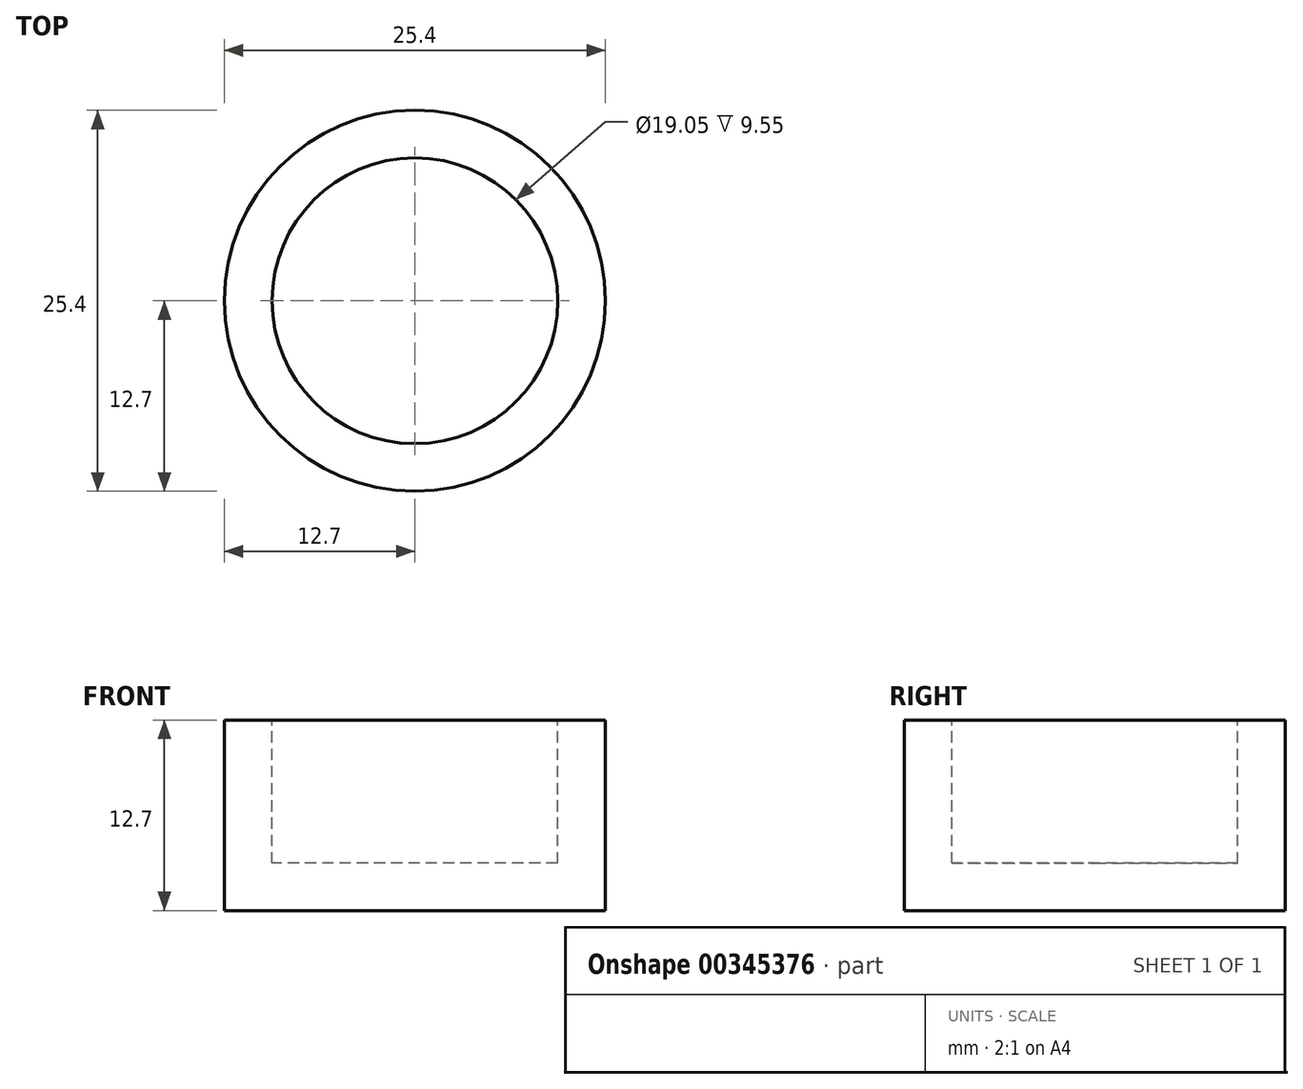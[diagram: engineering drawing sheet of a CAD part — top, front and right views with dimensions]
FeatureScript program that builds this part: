
annotation { "Feature Type Name" : "Feature", "Feature Type Description" : "" }
export const myFeature = defineFeature(function(context is Context, id is Id, definition is map)
    precondition{}
    {
        {
            var Q0;
            Q0=qCreatedBy(makeId("Top.planeOp"),FACE);
            var sketch = newSketch(context, id + "F0", { "sketchPlane" : qUnion([Q0])});
            skCircle(sketch, "E0", {"center": v(0, 0) * mm, "radius": 12.7 * mm});
            skSolve(sketch);
        }
        {
            var Q0;
            Q0 = qSketchRegion(id + "F0", true);
            extrude(context, id + "F1", {"entities" : qUnion([Q0]), "depth" : 12.7 * mm});
        }
        {
            var Q0;
            Q0=makeQuery(id+"F1.opExtrude","CAP_FACE",FACE,{"disambiguationData":[OSD([sQuery(id+"F0.wireOp",EDGE,"E0")])],"isStart":false});
            var sketch = newSketch(context, id + "F2", { "sketchPlane" : qUnion([Q0])});
            skCircle(sketch, "E1.0", {"center": v(0, 0) * mm, "radius": 12.7 * mm, "construction": true});
            skCircle(sketch, "E2.0", {"center": v(0, 0) * mm, "radius": 9.53 * mm});
            skSolve(sketch);
        }
        {
            var Q0;
            Q0 = qSketchRegion(id + "F2", true);
            extrude(context, id + "F3", {"entities" : qUnion([Q0]), "operationType" : NewBodyOperationType.REMOVE, "oppositeDirection" : true, "depth" : 9.55 * mm});
        }
    });
